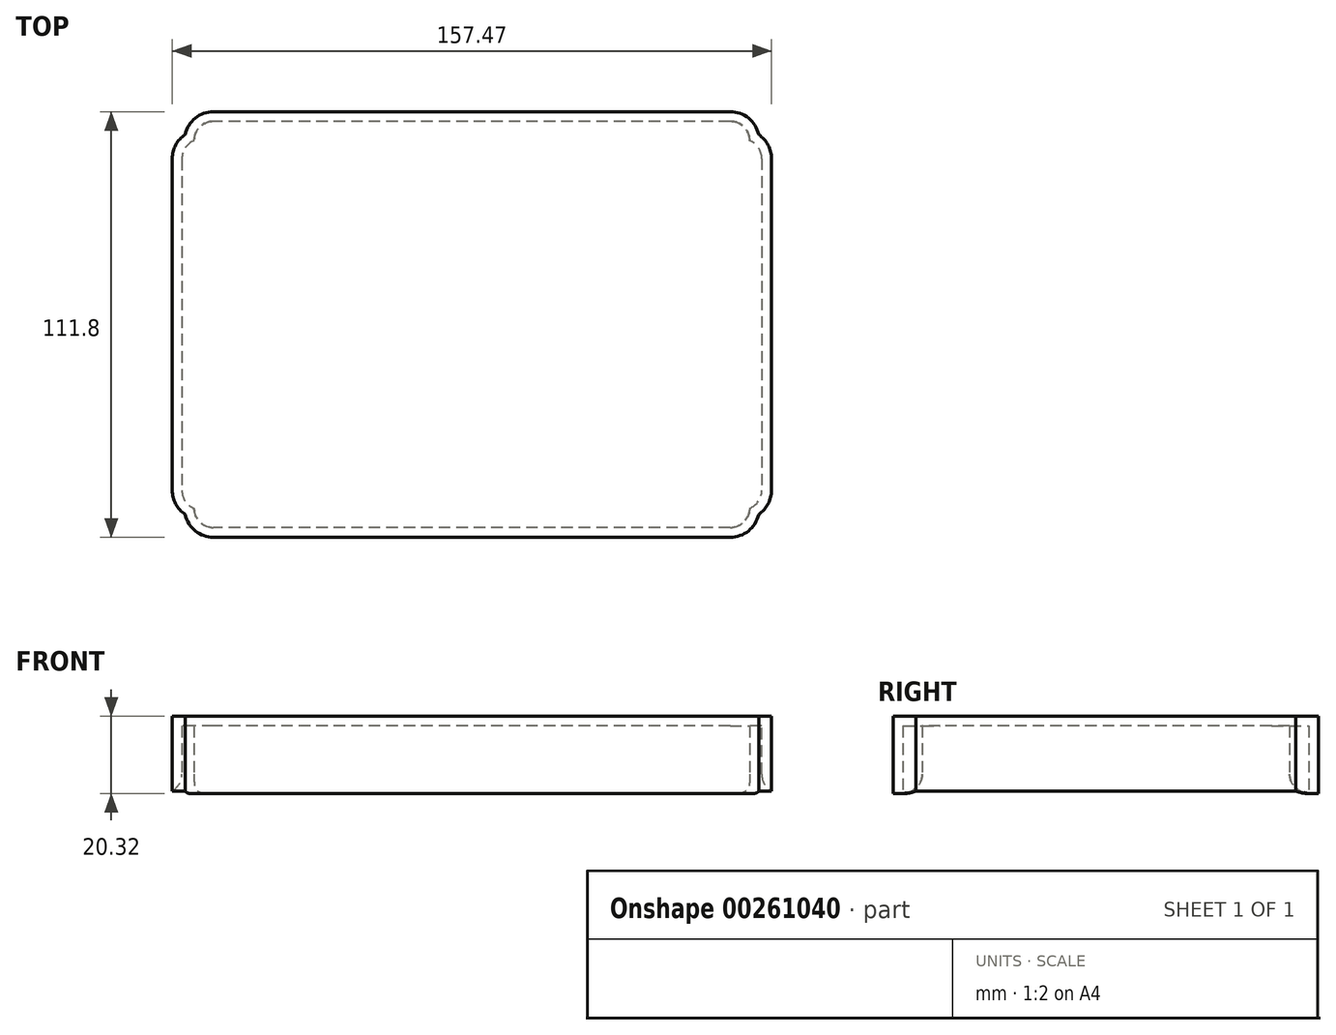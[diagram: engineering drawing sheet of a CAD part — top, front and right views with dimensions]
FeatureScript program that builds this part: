
annotation { "Feature Type Name" : "Feature", "Feature Type Description" : "" }
export const myFeature = defineFeature(function(context is Context, id is Id, definition is map)
    precondition{}
    {
        {
            var Q0;
            Q0=qCreatedBy(makeId("Top.planeOp"),FACE);
            var sketch = newSketch(context, id + "F0", { "sketchPlane" : qUnion([Q0])});
            skLineSegment(sketch, "E0.bottom", {"start": v(64.16, -53.53) * mm, "end": v(-71.65, -53.53) * mm});
            skLineSegment(sketch, "E0.top", {"start": v(64.16, 53.2) * mm, "end": v(-71.65, 53.2) * mm});
            skLineSegment(sketch, "E0.left", {"start": v(69.24, -48.45) * mm, "end": v(69.24, 48.11) * mm});
            skLineSegment(sketch, "E0.right", {"start": v(-76.73, -48.45) * mm, "end": v(-76.73, 48.11) * mm});
            skPoint(sketch, "E0.middle", {"position": v(-3.75, -0.17) * mm});
            skLineSegment(sketch, "E1.bottom", {"start": v(-71.65, -53.53) * mm, "end": v(64.16, -53.53) * mm});
            skLineSegment(sketch, "E1.top", {"start": v(-71.65, 53.2) * mm, "end": v(64.16, 53.2) * mm});
            skPoint(sketch, "E2.visualSharp", {"position": v(-76.73, 53.2) * mm});
            skArc(sketch, "E2.filletArc", {"start": v(-71.65, 53.2) * mm, "mid": v(-75.25, 51.7) * mm, "end": v(-76.73, 48.11) * mm});
            skPoint(sketch, "E3.visualSharp", {"position": v(69.24, 53.2) * mm});
            skArc(sketch, "E3.filletArc", {"start": v(69.24, 48.11) * mm, "mid": v(67.75, 51.7) * mm, "end": v(64.16, 53.2) * mm});
            skPoint(sketch, "E4.visualSharp", {"position": v(69.24, -53.53) * mm});
            skArc(sketch, "E4.filletArc", {"start": v(64.16, -53.53) * mm, "mid": v(67.75, -52.04) * mm, "end": v(69.24, -48.45) * mm});
            skPoint(sketch, "E5.visualSharp", {"position": v(-76.73, -53.53) * mm});
            skArc(sketch, "E5.filletArc", {"start": v(-76.73, -48.45) * mm, "mid": v(-75.25, -52.04) * mm, "end": v(-71.65, -53.53) * mm});
            skLineSegment(sketch, "E6.bottom", {"start": v(69.24, 48.11) * mm, "end": v(72.44, 48.11) * mm});
            skLineSegment(sketch, "E6.top", {"start": v(69.24, -48.45) * mm, "end": v(72.44, -48.45) * mm});
            skLineSegment(sketch, "E6.left", {"start": v(69.24, 48.11) * mm, "end": v(69.24, -48.45) * mm});
            skLineSegment(sketch, "E6.right", {"start": v(72.44, 48.11) * mm, "end": v(72.44, -48.45) * mm});
            skPoint(sketch, "E7.oppositeSnap0", {"position": v(70.84, -48.45) * mm});
            skLineSegment(sketch, "E7.bottom", {"start": v(-76.73, 48.11) * mm, "end": v(-79.95, 48.11) * mm});
            skLineSegment(sketch, "E7.top", {"start": v(-76.73, -48.45) * mm, "end": v(-79.95, -48.45) * mm});
            skLineSegment(sketch, "E7.left", {"start": v(-76.73, 48.11) * mm, "end": v(-76.73, -48.45) * mm});
            skLineSegment(sketch, "E7.right", {"start": v(-79.95, 48.11) * mm, "end": v(-79.95, -48.45) * mm});
            skLineSegment(sketch, "E8.top", {"start": v(-71.65, 55.84) * mm, "end": v(64.16, 55.84) * mm});
            skLineSegment(sketch, "E8.left", {"start": v(-71.65, 53.2) * mm, "end": v(-71.65, 55.84) * mm});
            skLineSegment(sketch, "E8.right", {"start": v(64.16, 53.2) * mm, "end": v(64.16, 55.84) * mm});
            skPoint(sketch, "E9.oppositeSnap0", {"position": v(64.16, 54.52) * mm});
            skLineSegment(sketch, "E9.top", {"start": v(-71.65, -56.18) * mm, "end": v(64.16, -56.18) * mm});
            skLineSegment(sketch, "E9.left", {"start": v(-71.65, -53.53) * mm, "end": v(-71.65, -56.18) * mm});
            skLineSegment(sketch, "E9.right", {"start": v(64.16, -53.53) * mm, "end": v(64.16, -56.18) * mm});
            skSolve(sketch);
        }
        {
            var Q0;
            Q0=makeQuery(id+"F0.imprint","IMPRINT",FACE,{"disambiguationData":[TD([[makeQuery(id+"F0.imprint","IMPRINT",EDGE,{"derivedFrom":sQuery(id+"F0.wireOp",EDGE,"E2.filletArc")}),1.0]])]});
            var Q1;
            Q1=makeQuery(id+"F0.imprint","IMPRINT",FACE,{"disambiguationData":[TD([[makeQuery(id+"F0.imprint","IMPRINT",EDGE,{"derivedFrom":sQuery(id+"F0.wireOp",EDGE,"E6.bottom")}),-1.0]])]});
            var Q2;
            Q2=makeQuery(id+"F0.imprint","IMPRINT",FACE,{"disambiguationData":[TD([[makeQuery(id+"F0.imprint","IMPRINT",EDGE,{"derivedFrom":sQuery(id+"F0.wireOp",EDGE,"E1.bottom")}),-1.0]])]});
            var Q3;
            Q3=makeQuery(id+"F0.imprint","IMPRINT",FACE,{"disambiguationData":[TD([[makeQuery(id+"F0.imprint","IMPRINT",EDGE,{"derivedFrom":sQuery(id+"F0.wireOp",EDGE,"E1.top")}),1.0]])]});
            var Q4;
            Q4=makeQuery(id+"F0.imprint","IMPRINT",FACE,{"disambiguationData":[TD([[makeQuery(id+"F0.imprint","IMPRINT",EDGE,{"derivedFrom":sQuery(id+"F0.wireOp",EDGE,"E7.bottom")}),1.0]])]});
            extrude(context, id + "F1", {"entities" : qUnion([Q0, Q1, Q2, Q3, Q4]), "depth" : 17.78 * mm});
        }
        {
            var Q0;
            Q0=makeQuery(id+"F1.opExtrude","SWEPT_EDGE",EDGE,{"disambiguationData":[OSD([sQuery(id+"F0.wireOp",EDGE,"E6.top"),sQuery(id+"F0.wireOp",EDGE,"E6.right")])]});
            var Q1;
            Q1=makeQuery(id+"F1.opExtrude","SWEPT_EDGE",EDGE,{"disambiguationData":[OSD([sQuery(id+"F0.wireOp",EDGE,"E9.top"),sQuery(id+"F0.wireOp",EDGE,"E9.right")])]});
            var Q2;
            Q2=makeQuery(id+"F1.opExtrude","SWEPT_EDGE",EDGE,{"disambiguationData":[OSD([sQuery(id+"F0.wireOp",EDGE,"E8.top"),sQuery(id+"F0.wireOp",EDGE,"E8.right")])]});
            var Q3;
            Q3=makeQuery(id+"F1.opExtrude","SWEPT_EDGE",EDGE,{"disambiguationData":[OSD([sQuery(id+"F0.wireOp",EDGE,"E6.bottom"),sQuery(id+"F0.wireOp",EDGE,"E6.right")])]});
            var Q4;
            Q4=makeQuery(id+"F1.opExtrude","SWEPT_EDGE",EDGE,{"disambiguationData":[OSD([sQuery(id+"F0.wireOp",EDGE,"E8.top"),sQuery(id+"F0.wireOp",EDGE,"E8.left")])]});
            var Q5;
            Q5=makeQuery(id+"F1.opExtrude","SWEPT_EDGE",EDGE,{"disambiguationData":[OSD([sQuery(id+"F0.wireOp",EDGE,"E7.bottom"),sQuery(id+"F0.wireOp",EDGE,"E7.right")])]});
            var Q6;
            Q6=makeQuery(id+"F1.opExtrude","SWEPT_EDGE",EDGE,{"disambiguationData":[OSD([sQuery(id+"F0.wireOp",EDGE,"E7.top"),sQuery(id+"F0.wireOp",EDGE,"E7.right")])]});
            var Q7;
            Q7=makeQuery(id+"F1.opExtrude","SWEPT_EDGE",EDGE,{"disambiguationData":[OSD([sQuery(id+"F0.wireOp",EDGE,"E9.top"),sQuery(id+"F0.wireOp",EDGE,"E9.left")])]});
            fillet(context, id + "F2", {"entities" : qUnion([Q0, Q1, Q2, Q3, Q4, Q5, Q6, Q7]), "radius" : 5.08 * mm, "tangentPropagation" : true, "allowEdgeOverflow" : false});
        }
        {
            var Q0;
            Q0=makeQuery(id+"F1.opExtrude","CAP_FACE",FACE,{"disambiguationData":[OSD([sQuery(id+"F0.wireOp",EDGE,"E2.filletArc"),sQuery(id+"F0.wireOp",EDGE,"E3.filletArc"),sQuery(id+"F0.wireOp",EDGE,"E4.filletArc"),sQuery(id+"F0.wireOp",EDGE,"E5.filletArc"),sQuery(id+"F0.wireOp",EDGE,"E6.bottom"),sQuery(id+"F0.wireOp",EDGE,"E6.top"),sQuery(id+"F0.wireOp",EDGE,"E6.right"),sQuery(id+"F0.wireOp",EDGE,"E7.bottom"),sQuery(id+"F0.wireOp",EDGE,"E7.top"),sQuery(id+"F0.wireOp",EDGE,"E7.right"),sQuery(id+"F0.wireOp",EDGE,"E8.top"),sQuery(id+"F0.wireOp",EDGE,"E8.left"),sQuery(id+"F0.wireOp",EDGE,"E8.right"),sQuery(id+"F0.wireOp",EDGE,"E9.top"),sQuery(id+"F0.wireOp",EDGE,"E9.left"),sQuery(id+"F0.wireOp",EDGE,"E9.right")])],"isStart":true});
            shell(context, id + "F3", {"entities" : qUnion([Q0]), "thickness" : 2.54 * mm, "oppositeDirection" : true});
        }
        {
            var Q0;
            {var subQ0=sQuery(id+"F0.wireOp",EDGE,"E9.top");Q0=makeQuery(id+"F3.opShell","OFFSET_EDGE",EDGE,{"disambiguationData":[OSD([subQ0]),TDD([makeQuery(id+"F1.opExtrude","CAP_EDGE",EDGE,{"disambiguationData":[OSD([subQ0])],"isStart":true})])]});}
            var Q1;
            {var subQ0=sQuery(id+"F0.wireOp",EDGE,"E7.right");Q1=makeQuery(id+"F3.opShell","OFFSET_EDGE",EDGE,{"disambiguationData":[OSD([subQ0]),TDD([makeQuery(id+"F1.opExtrude","CAP_EDGE",EDGE,{"disambiguationData":[OSD([subQ0])],"isStart":true})])]});}
            var Q2;
            {var subQ0=sQuery(id+"F0.wireOp",EDGE,"E6.right");Q2=makeQuery(id+"F3.opShell","OFFSET_EDGE",EDGE,{"disambiguationData":[OSD([subQ0]),TDD([makeQuery(id+"F1.opExtrude","CAP_EDGE",EDGE,{"disambiguationData":[OSD([subQ0])],"isStart":true})])]});}
            var Q3;
            {var subQ0=sQuery(id+"F0.wireOp",EDGE,"E8.top");Q3=makeQuery(id+"F3.opShell","OFFSET_EDGE",EDGE,{"disambiguationData":[OSD([subQ0]),TDD([makeQuery(id+"F1.opExtrude","CAP_EDGE",EDGE,{"disambiguationData":[OSD([subQ0])],"isStart":true})])]});}
            fillet(context, id + "F4", {"entities" : qUnion([Q0, Q1, Q2, Q3]), "radius" : 5.08 * mm, "tangentPropagation" : true, "allowEdgeOverflow" : false});
        }
    });
